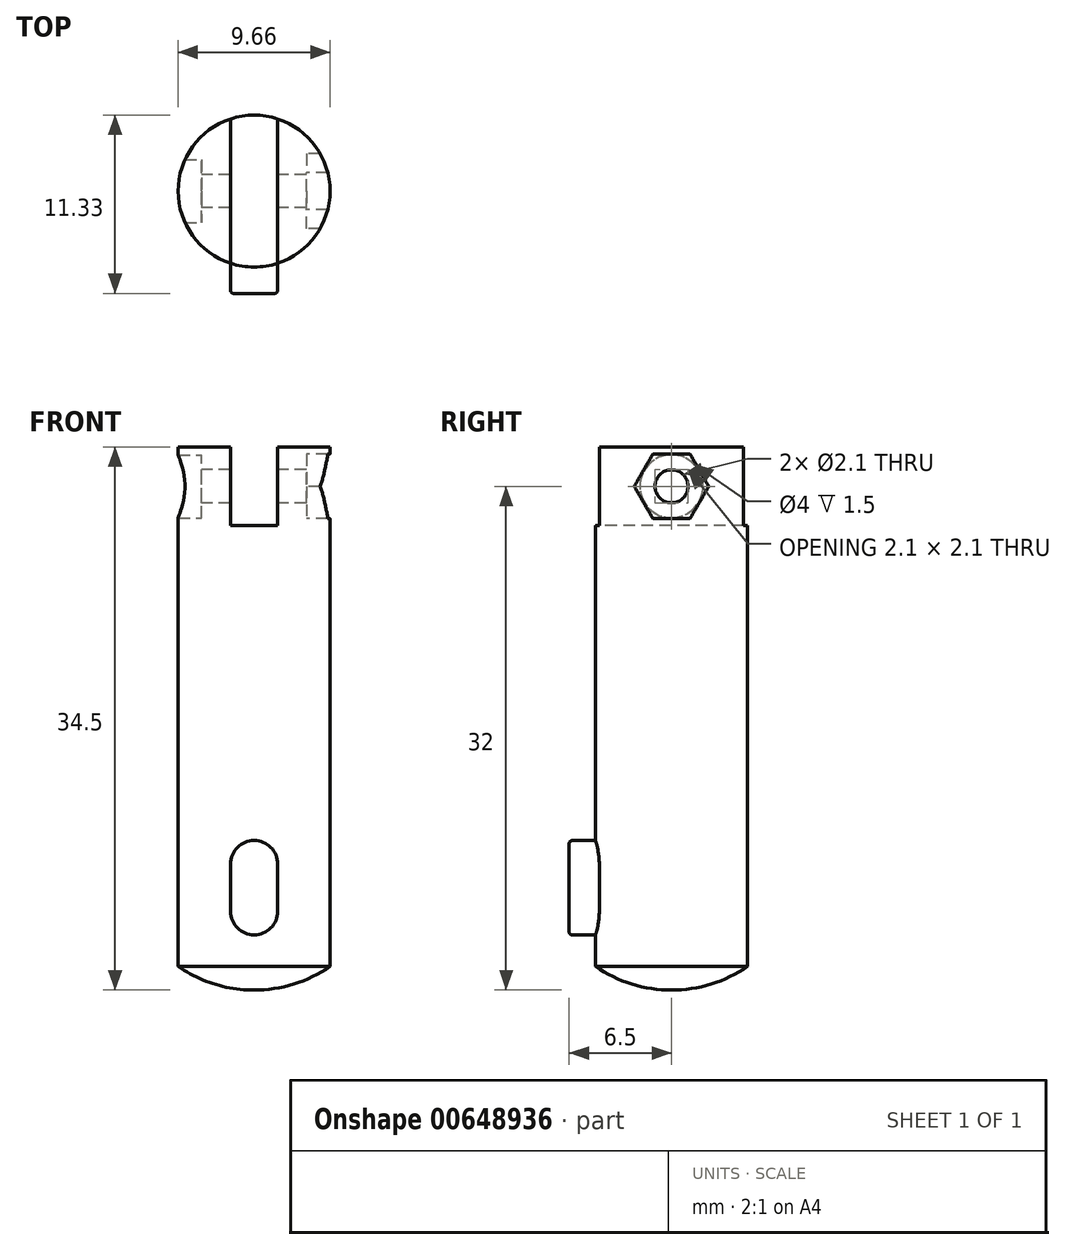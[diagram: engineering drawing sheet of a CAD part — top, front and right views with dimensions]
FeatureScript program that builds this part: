
annotation { "Feature Type Name" : "Feature", "Feature Type Description" : "" }
export const myFeature = defineFeature(function(context is Context, id is Id, definition is map)
    precondition{}
    {
        {
            var Q0;
            Q0=qCreatedBy(makeId("Top.planeOp"),FACE);
            var sketch = newSketch(context, id + "F0", { "sketchPlane" : qUnion([Q0])});
            skCircle(sketch, "E0", {"center": v(0, 0) * mm, "radius": 4.83 * mm});
            skSolve(sketch);
        }
        {
            var Q0;
            Q0=qSketchRegion(id+"F0",true);
            extrude(context, id + "F1", {"entities" : qUnion([Q0]), "depth" : 33 * mm});
        }
        {
            var Q0;
            Q0=qCreatedBy(makeId("Front.planeOp"),FACE);
            var sketch = newSketch(context, id + "F2", { "sketchPlane" : qUnion([Q0])});
            skLineSegment(sketch, "E1", {"start": v(0, 3.5) * mm, "end": v(0, 6.5) * mm, "construction": true});
            skArc(sketch, "E2.0.startCap", {"start": v(1.5, 3.5) * mm, "mid": v(0, 2) * mm, "end": v(-1.5, 3.5) * mm});
            skArc(sketch, "E2.0.endCap", {"start": v(-1.5, 6.5) * mm, "mid": v(0, 8) * mm, "end": v(1.5, 6.5) * mm});
            skLineSegment(sketch, "E2.0.left", {"start": v(-1.5, 3.5) * mm, "end": v(-1.5, 6.5) * mm});
            skLineSegment(sketch, "E2.0.right", {"start": v(1.5, 3.5) * mm, "end": v(1.5, 6.5) * mm});
            skSolve(sketch);
        }
        {
            var Q0;
            Q0=qSketchRegion(id+"F2",true);
            var Q1;
            Q1=qBodyType(qCreatedBy(id+"F2",EDGE),BodyType.WIRE);
            extrude(context, id + "F3", {"entities" : qUnion([Q0]), "operationType" : NewBodyOperationType.ADD, "surfaceEntities" : qUnion([Q1]), "depth" : 6.5 * mm});
        }
        {
            var Q0;
            Q0=makeQuery(id+"F3.opExtrude","CAP_FACE",FACE,{"disambiguationData":[OSD([sQuery(id+"F2.wireOp",EDGE,"E2.0.startCap"),sQuery(id+"F2.wireOp",EDGE,"E2.0.endCap"),sQuery(id+"F2.wireOp",EDGE,"E2.0.left"),sQuery(id+"F2.wireOp",EDGE,"E2.0.right")])],"isStart":false});
            fillet(context, id + "F4", {"entities" : qUnion([Q0]), "radius" : 0.2 * mm, "tangentPropagation" : true, "allowEdgeOverflow" : false});
        }
        {
            var Q0;
            Q0=qCreatedBy(makeId("Front.planeOp"),FACE);
            var sketch = newSketch(context, id + "F5", { "sketchPlane" : qUnion([Q0])});
            skLineSegment(sketch, "E3", {"start": v(0, 0) * mm, "end": v(0, -2.82) * mm, "construction": true});
            skLineSegment(sketch, "E4", {"start": v(-4.62, -1.5) * mm, "end": v(4.9, -1.5) * mm, "construction": true});
            skLineSegment(sketch, "E5.0", {"start": v(-4.83, 0) * mm, "end": v(0, 0) * mm});
            skArc(sketch, "E6", {"start": v(-4.83, 0) * mm, "mid": v(-2.53, -1.12) * mm, "end": v(0, -1.5) * mm});
            skLineSegment(sketch, "E7", {"start": v(0, 0) * mm, "end": v(0, -1.5) * mm});
            skPoint(sketch, "E8.orphan", {"position": v(4.83, 0) * mm});
            skSolve(sketch);
        }
        {
            var Q0;
            Q0=qSketchRegion(id+"F5",true);
            var Q1;
            Q1=sQuery(id+"F5.wireOp",EDGE,"E3");
            revolve(context, id + "F6", {"operationType" : NewBodyOperationType.ADD, "entities" : qUnion([Q0]), "axis" : qUnion([Q1]), "revolveType" : RevolveType.FULL});
        }
        {
            var Q0;
            Q0=makeQuery(id+"F1.opExtrude","CAP_FACE",FACE,{"disambiguationData":[OSD([sQuery(id+"F0.wireOp",EDGE,"E0")])],"isStart":false});
            var sketch = newSketch(context, id + "F7", { "sketchPlane" : qUnion([Q0])});
            skLineSegment(sketch, "E9", {"start": v(0, 11.02) * mm, "end": v(0, -10.17) * mm, "construction": true});
            skLineSegment(sketch, "E10.0", {"start": v(-1.5, 4.59) * mm, "end": v(-1.5, -4.59) * mm});
            skLineSegment(sketch, "E11.0", {"start": v(1.5, 4.59) * mm, "end": v(1.5, -4.59) * mm});
            skArc(sketch, "E12.0", {"start": v(1.5, 4.59) * mm, "mid": v(0, 4.83) * mm, "end": v(-1.5, 4.59) * mm});
            skArc(sketch, "E13.trimOffspring", {"start": v(-1.5, -4.59) * mm, "mid": v(0, -4.83) * mm, "end": v(1.5, -4.59) * mm});
            skSolve(sketch);
        }
        {
            var Q0;
            Q0=qSketchRegion(id+"F7",true);
            extrude(context, id + "F8", {"entities" : qUnion([Q0]), "operationType" : NewBodyOperationType.REMOVE, "oppositeDirection" : true, "depth" : 5 * mm});
        }
        {
            var Q0;
            Q0=qCreatedBy(makeId("Right.planeOp"),FACE);
            var sketch = newSketch(context, id + "F9", { "sketchPlane" : qUnion([Q0])});
            skCircle(sketch, "E14", {"center": v(0, 30.5) * mm, "radius": 1.05 * mm});
            skSolve(sketch);
        }
        {
            var Q0;
            Q0=qSketchRegion(id+"F9",true);
            extrude(context, id + "F10", {"entities" : qUnion([Q0]), "operationType" : NewBodyOperationType.REMOVE, "endBound" : BoundingType.THROUGH_ALL, "depth" : 25 * mm, "hasSecondDirection" : true, "secondDirectionBound" : SecondDirectionBoundingType.THROUGH_ALL, "secondDirectionOppositeDirection" : true, "secondDirectionDepth" : 25 * mm});
        }
        {
            var Q0;
            Q0=qCreatedBy(makeId("Right.planeOp"),FACE);
            var sketch = newSketch(context, id + "F11", { "sketchPlane" : qUnion([Q0])});
            skCircle(sketch, "E15.0", {"center": v(0, 30.5) * mm, "radius": 1.05 * mm, "construction": true});
            skCircle(sketch, "E16.cCircle", {"center": v(0, 30.5) * mm, "radius": 2.05 * mm, "construction": true});
            skLineSegment(sketch, "E16.0", {"start": v(2.37, 30.5) * mm, "end": v(1.18, 28.45) * mm});
            skLineSegment(sketch, "E16.1", {"start": v(1.18, 28.45) * mm, "end": v(-1.18, 28.45) * mm});
            skLineSegment(sketch, "E16.2", {"start": v(-1.18, 28.45) * mm, "end": v(-2.37, 30.5) * mm});
            skLineSegment(sketch, "E16.3", {"start": v(-2.37, 30.5) * mm, "end": v(-1.18, 32.55) * mm});
            skLineSegment(sketch, "E16.4", {"start": v(-1.18, 32.55) * mm, "end": v(1.18, 32.55) * mm});
            skLineSegment(sketch, "E16.5", {"start": v(1.18, 32.55) * mm, "end": v(2.37, 30.5) * mm});
            skPoint(sketch, "E16.0.midPoint", {"position": v(1.78, 29.48) * mm});
            skLineSegment(sketch, "E17.0", {"start": v(-4.59, 33) * mm, "end": v(4.59, 33) * mm, "construction": true});
            skSolve(sketch);
        }
        {
            var Q0;
            Q0=qSketchRegion(id+"F11",true);
            extrude(context, id + "F12", {"entities" : qUnion([Q0]), "operationType" : NewBodyOperationType.REMOVE, "endBound" : BoundingType.THROUGH_ALL, "depth" : 25 * mm, "hasSecondDirection" : true, "secondDirectionOppositeDirection" : false, "secondDirectionDepth" : 3.33 * mm});
        }
        {
            var Q0;
            Q0=qCreatedBy(makeId("Right.planeOp"),FACE);
            var sketch = newSketch(context, id + "F13", { "sketchPlane" : qUnion([Q0])});
            skCircle(sketch, "E18.0", {"center": v(0, 30.5) * mm, "radius": 1.05 * mm, "construction": true});
            skCircle(sketch, "E19", {"center": v(0, 30.5) * mm, "radius": 2 * mm});
            skSolve(sketch);
        }
        {
            var Q0;
            Q0=qSketchRegion(id+"F13",true);
            extrude(context, id + "F14", {"entities" : qUnion([Q0]), "operationType" : NewBodyOperationType.REMOVE, "endBound" : BoundingType.THROUGH_ALL, "oppositeDirection" : true, "depth" : 25 * mm, "hasSecondDirection" : true, "secondDirectionOppositeDirection" : true, "secondDirectionDepth" : 3.33 * mm});
        }
    });
